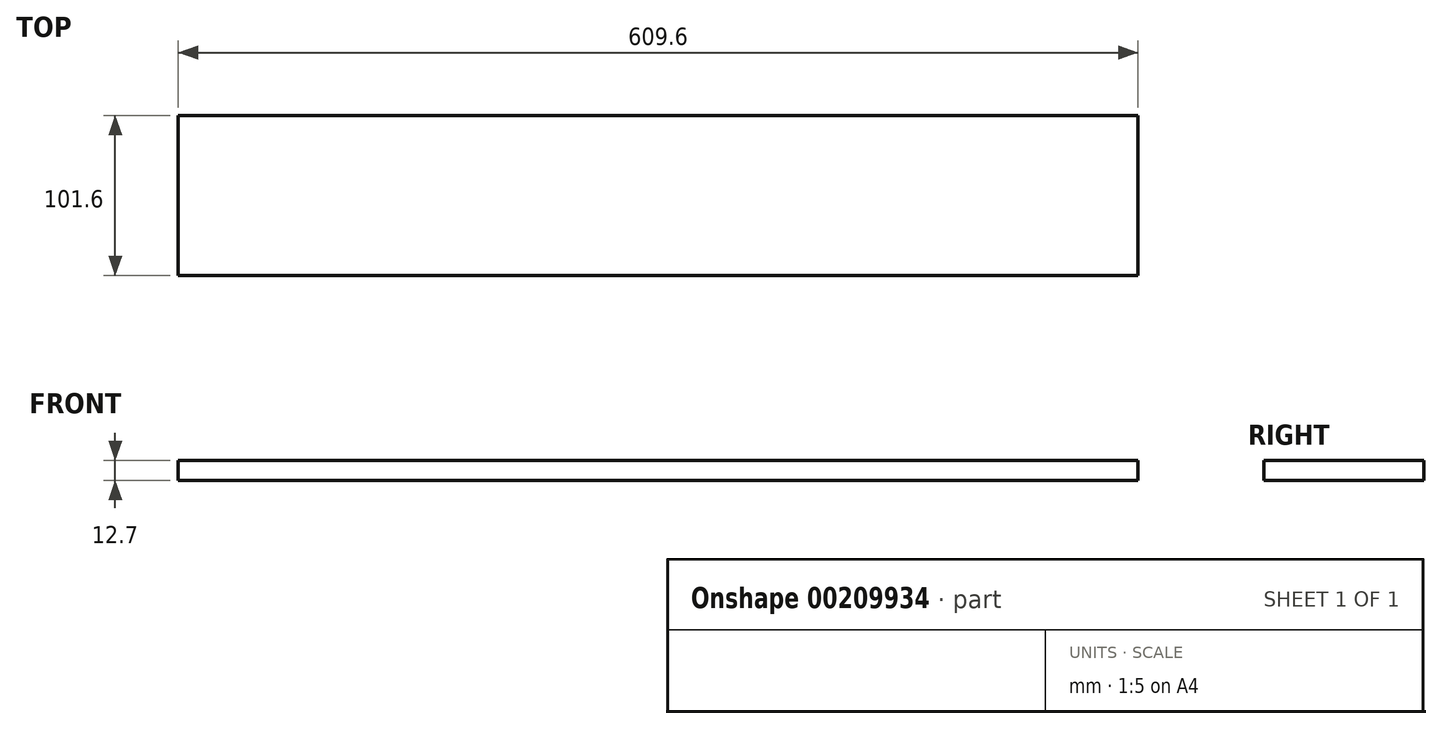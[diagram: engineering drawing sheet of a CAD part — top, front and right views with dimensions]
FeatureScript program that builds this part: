
annotation { "Feature Type Name" : "Feature", "Feature Type Description" : "" }
export const myFeature = defineFeature(function(context is Context, id is Id, definition is map)
    precondition{}
    {
        {
            var Q0;
            Q0=qCreatedBy(makeId("Top.planeOp"),FACE);
            var sketch = newSketch(context, id + "F0", { "sketchPlane" : qUnion([Q0])});
            skLineSegment(sketch, "E0.bottom", {"start": v(-304.8, 50.8) * mm, "end": v(304.8, 50.8) * mm});
            skLineSegment(sketch, "E0.top", {"start": v(-304.8, -50.8) * mm, "end": v(304.8, -50.8) * mm});
            skLineSegment(sketch, "E0.left", {"start": v(-304.8, 50.8) * mm, "end": v(-304.8, -50.8) * mm});
            skLineSegment(sketch, "E0.right", {"start": v(304.8, 50.8) * mm, "end": v(304.8, -50.8) * mm});
            skPoint(sketch, "E0.middle", {"position": v(0, 0) * mm});
            skSolve(sketch);
        }
        {
            var Q0;
            Q0=makeQuery(id+"F0.imprint","IMPRINT",FACE,{"disambiguationData":[TD([[makeQuery(id+"F0.imprint","IMPRINT",EDGE,{"derivedFrom":sQuery(id+"F0.wireOp",EDGE,"E0.bottom")}),-1.0]])]});
            extrude(context, id + "F1", {"entities" : qUnion([Q0]), "depth" : 12.7 * mm});
        }
    });
